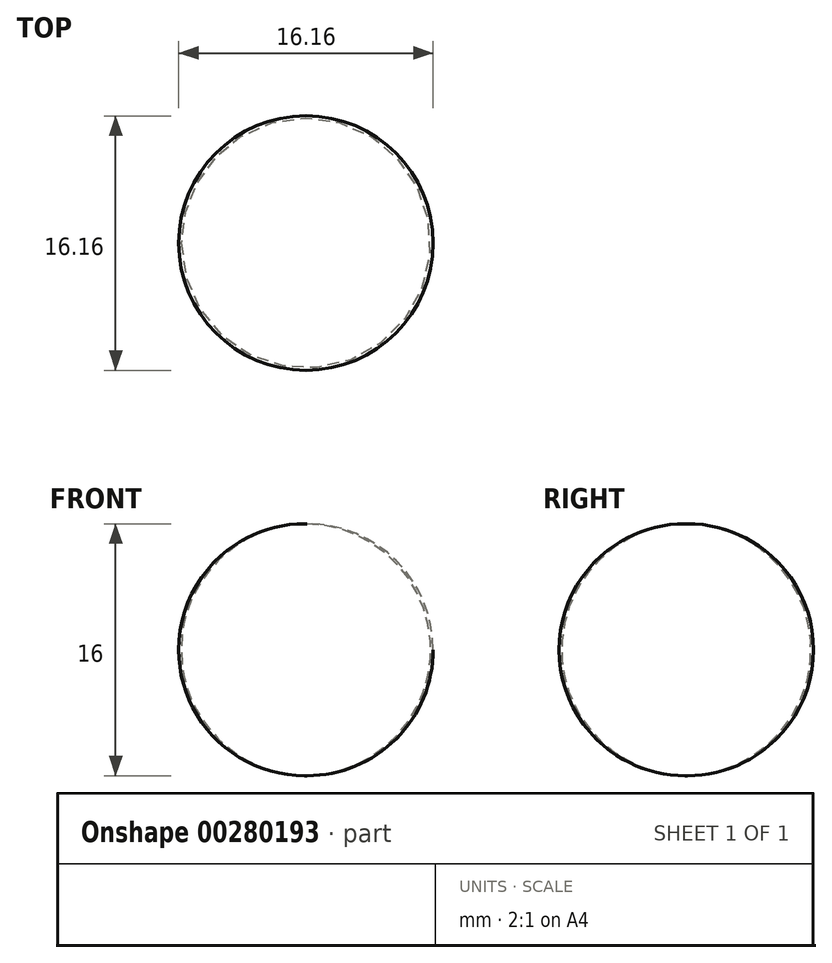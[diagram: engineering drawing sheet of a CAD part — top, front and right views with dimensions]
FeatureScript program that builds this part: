
annotation { "Feature Type Name" : "Feature", "Feature Type Description" : "" }
export const myFeature = defineFeature(function(context is Context, id is Id, definition is map)
    precondition{}
    {
        {
            var Q0;
            Q0=qCreatedBy(makeId("Front.planeOp"),FACE);
            var sketch = newSketch(context, id + "F0", { "sketchPlane" : qUnion([Q0])});
            skLineSegment(sketch, "E0", {"start": v(0, 16) * mm, "end": v(0, 0) * mm});
            skArc(sketch, "E1", {"start": v(0, 0) * mm, "mid": v(8.08, 8) * mm, "end": v(0, 16) * mm});
            skSolve(sketch);
        }
        {
            var Q0;
            Q0=makeQuery(id+"F0.imprint","IMPRINT",FACE,{"disambiguationData":[TD([[makeQuery(id+"F0.imprint","IMPRINT",EDGE,{"derivedFrom":sQuery(id+"F0.wireOp",EDGE,"E0")}),1.0]])]});
            var Q1;
            Q1=sQuery(id+"F0.wireOp",EDGE,"E0");
            revolve(context, id + "F1", {"entities" : qUnion([Q0]), "axis" : qUnion([Q1]), "revolveType" : RevolveType.FULL});
        }
    });
